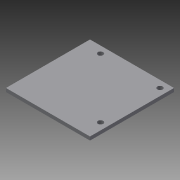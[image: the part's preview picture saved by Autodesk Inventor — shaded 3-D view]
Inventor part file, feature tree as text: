
AUTODESK INVENTOR PART (.ipt)
format: ipt  version: 2015 (Build 190159000, 159)  size: 83,968 bytes
history: native  units: mm
features: extrude x1, sketch x1
ambient origin geometry x8: Origin, YZ Plane, XZ Plane, XY Plane, X Axis, Y Axis, Z Axis, Center Point
bodies: Solid1 (feature_tree)
feature tree (2):
  extrude  "Extrusion1"  Depth=48.0mm
  sketch  "Sketch1"  dims[d0=48.0mm d1=48.0mm d2=4.0mm d3=4.0mm d4=3.0mm d5=4.0mm d6=10.0mm d7=3.0mm d8=10.0mm d9=4.0mm d10=3.0mm d11=2.0mm d12=0.0mm]
